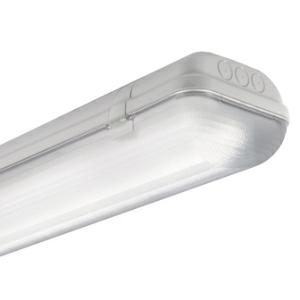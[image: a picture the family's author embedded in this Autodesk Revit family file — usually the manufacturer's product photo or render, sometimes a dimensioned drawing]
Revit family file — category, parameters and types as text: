
# Revit family: 3f_filippi_-_3f_linda_basic_3f_filippi_-_58765_-_3f_linda_led_basic_2x23w_l1570
name_source: partatom
category: Lighting Fixtures
units: mm (PartAtom-declared; Revit-internal decimal feet)

## family parameters
Cut with Voids When Loaded = No
Host = Face
Light Source = No
Part Type = Normal
Room Calculation Point = No
Round Connector Dimension = Use Diameter
Shared = No

## types (1)
- 3F Filippi - 3F Linda Basic (1 x LED, 6905 lm, 46 W, 4000 K)
    Apparent Load = 46 VA
    Approval mark = CE
    CIE Flux Codes = 46 76 93 97 100
    Color Rendering = 80
    Color Temperature = 4000 K
    Control Gear = Electronic ballast
    Default Elevation = 1800 mm
    Description = ILLUMINOTECHNICAL
Luminous efficiency 100% (DLOR 97%, ULOR 3%).
Initial luminous flux of the luminaire 6905 lm.
Controlled direct symmetric distribution.
Installation Interdistance Transv.D = 1.35 x hu - Long.D = 1.24 x hu.
Tabular UGR (CIE 117 - 4H-8H; S=0.25H; 70/50/20): RUG 23.2 - 22.4.
Beam angle: 94° - 78°.
Luminous efficacy 150 lm/W.
Lifetime (L92/B10): 30000 h. (tq+25°C)
Lifetime (L85/B10): 50000 h. (tq+25°C)
Lifetime (L75/B10): 80000 h. (tq+25°C)
Lifetime (L70/B10): 100000 h. (tq+25°C)
Lifetime (L75/B10): 50000 h. (tq+40°C)
Sudden decreased luminous flux after 50000 hours: 0% (C0).
Photobiological safety in compliance with IEC/TR 62778: RG0 risk exempt, (IEC 62471).
In compliance with IEC/EN 62722-2-1 - IEC/EN 62717 standards.

SOURCE
2 linear LED modules 23W/840.
Energy efficiency class (UE 2019/2020 - UE 2019/2015): D.
CIE 13.3 Colour rendering index: CRI >80 (R9 <50%).
IES TM-30 Fidelity Index: Rf = 84 Rg = 95.
CCT nominal colour temperature 4000 K.
Colour initial tolerance (MacAdam): SDCM 3.

MECHANICAL
Self-extinguishing V2 polycarbonate housing, injection moulded, RAL 7035 grey.
Ecologic anti-aging injected sealing gasket.
Diffuser in self-extinguishing V2 polycarbonate, photo-engraved interior, UV stabilised, injection moulded with smooth outer surface, tamper-proof opening.
Gear-holder reflector in hot-dip galvanised steel, painted with white polyester base.
Snug fit snap-lock clips for diffuser mounting, in polycarbonate.
Fixing brackets in stainless steel.
Possibility for technicians to access the interior of the luminaire.
Luminaire with limited surface temperature. - D - (EN 60598-2-24)
Dimensions: 1570x160 mm, height 100 mm. Weight 3.24 kg.
IP66 protection degree.
Mechanical strength to impacts IK10 (20 joule).
Glow-wire test resistance 850°C.

ELECTRICAL
Halogen Free electronic wiring 230V-50/60Hz, power factor 0.95, THD <25%, constant output current, SELV, class I, 1 driver.
Power of the luminaire 46 W.
ENEC - CE.
SAFE FLICKER: PstLM=<1 and SVM=<0.4 (IEC TR 61547-1 and IEC TR 63158), to ensure a more comfortable and safe light.
Luminaire compliant with EN 60598-2-22 for power supply from a centralised emergency system CPSS (Central Power Supply System), not incorporated in the luminaire - high risk areas excluded. The default power and flux are 100% in AC and 100% in DC.
Ambient temperature from -20°C to +40°C.
Temperature class T6 max 85°C.
Relative humidity UR: <85%.

INSTALLATION
Ceiling / Suspended / Wall.
All accessories dedicated to this product are available on the Catalog and on our website www.3F-Filippi.com.

APPLICATIONS
Suitable product for food production plants (HACCP), IFS (Food Version 6), BRC (GSFS Food Version 7).
Dry, dusty indoor environments, subject to occasional water splashes.
Virtually shatterproof polycarbonate compatibly with the fumes / atmospheres that compromise the elasticity of plastic materials.
Not suitable for installation on surfaces subject to important vibrations, exposed to weather conditions, on ropes or poles.
Suitable for illumination of public car parks and parking grounds referred to DIN 67528:2018-04.

WARNING
Fixture not suitable for cold stores with an ambient temperature <0°C and/or relative humidity >85%.
Luminaire designed for disposal/recycling at end-of-life.
Replaceable (LED only) light source by a professional. Replaceable control gear by a professional.
    Height = 100 mm  [stored 0.328084 ft]
    Lamp = 1 x LED
    Lamp Light Flux = 6905 lm
    Lamp Power = 46 W
    Lamp count = 1
    Length = 1570 mm
    Lifetime = 50000 h
    Luminous efficacy = 150 lm/W
    Manufacturer = 3F Filippi
    ModVariant = No
    Model = 3F Filippi - 58765 - 3F Linda LED Basic 2x23W L1570
    Mounting Place = Ceiling
    Mounting Type = Pendant
    Number of Poles = 1
    OnlyDefault = Yes
    Power Factor = 1
    Product Name = 3F Filippi - 3F Linda Basic
    Product group = pendant luminaire
    ProductGroupID = 9
    Protection Class = Protection class I
    Protection Degree = IP 66
    RLX_Detail_Level = 1
    RLX_Emergency_Light_Flux = 0 lm
    RLX_Emergency_Type = 0
    RLX_Emergency_Type_DB = No
    RlxData = <blob elided: 70513 chars, md5=eb140232>
    Socket = socket
    Standby Power = 0 W
    System Light Flux = 6905 lm
    System Power = 46 W
    Type Comments = Product without accessories
    Type Image = 3ffilippi_3f_linda_led_basic_2x.jpg
    URL = http://relux.com
    VarID = ---
    Voltage = 0 V
    Weight = 0.00 kg
    Width = 160 mm

note: [stored X ft] marks values corroborated as IEEE doubles in the binary element streams (Revit-internal decimal feet)

## geometry (parser evidence)
native form markers: Blend x4, Sweep x9
no freeform markers — native parametric forms only
